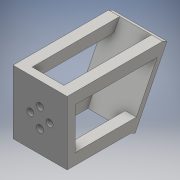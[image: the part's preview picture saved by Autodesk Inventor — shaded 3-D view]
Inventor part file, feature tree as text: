
AUTODESK INVENTOR PART (.ipt)
format: ipt  version: 2016 (Build 200138000, 138)  size: 174,080 bytes
history: native  units: mm
features: sketch x6, extrude x5, hole x1
ambient origin geometry x8: Origin, YZ Plane, XZ Plane, XY Plane, X Axis, Y Axis, Z Axis, Center Point
bodies: Solid1 (feature_tree)
feature tree (12):
  extrude  "Extrusion1"  Depth=40.0mm
  extrude  "Extrusion2"  Depth=3.0mm
  hole  "Hole1"  [1 undecoded]
  extrude  "Extrusion3"  Depth=4.35mm
  extrude  "Extrusion4"  Depth=4.35mm
  extrude  "Extrusion5"  Depth=3.0mm
  sketch  "Sketch1"  dims[d0=34.0mm d1=40.0mm]
  sketch  "Sketch2"  dims[d2=3.0mm d3=0.0mm d4=18.0mm]
  sketch  "Sketch4"  dims[d5=2.0mm d6=0.0mm d7=6.0mm]
  sketch  "Sketch5"  dims[d8=4.35mm d9=4.35mm]
  sketch  "Sketch6"  dims[d10=12.0mm d11=4.35mm]
  sketch  "Sketch7"  dims[d12=6.0mm d13=4.35mm d14=12.0mm d15=4.35mm d16=6.0mm d17=4.0mm d18=2.0mm d19=90.0deg d20=8.0mm d21=20.594885mm d22=7.0mm d23=7.0mm d24=7.0mm d25=7.0mm d26=55.0mm d27=0.0mm d28=20.0mm d29=0.0mm d30=0.0mm d31=3.0mm d32=0.0mm]
note: 1 required parameter value undecoded (feature->parameter linkage not recoverable at this tier; creation-order binding heuristic only, values carry confidence <= 0.55)
